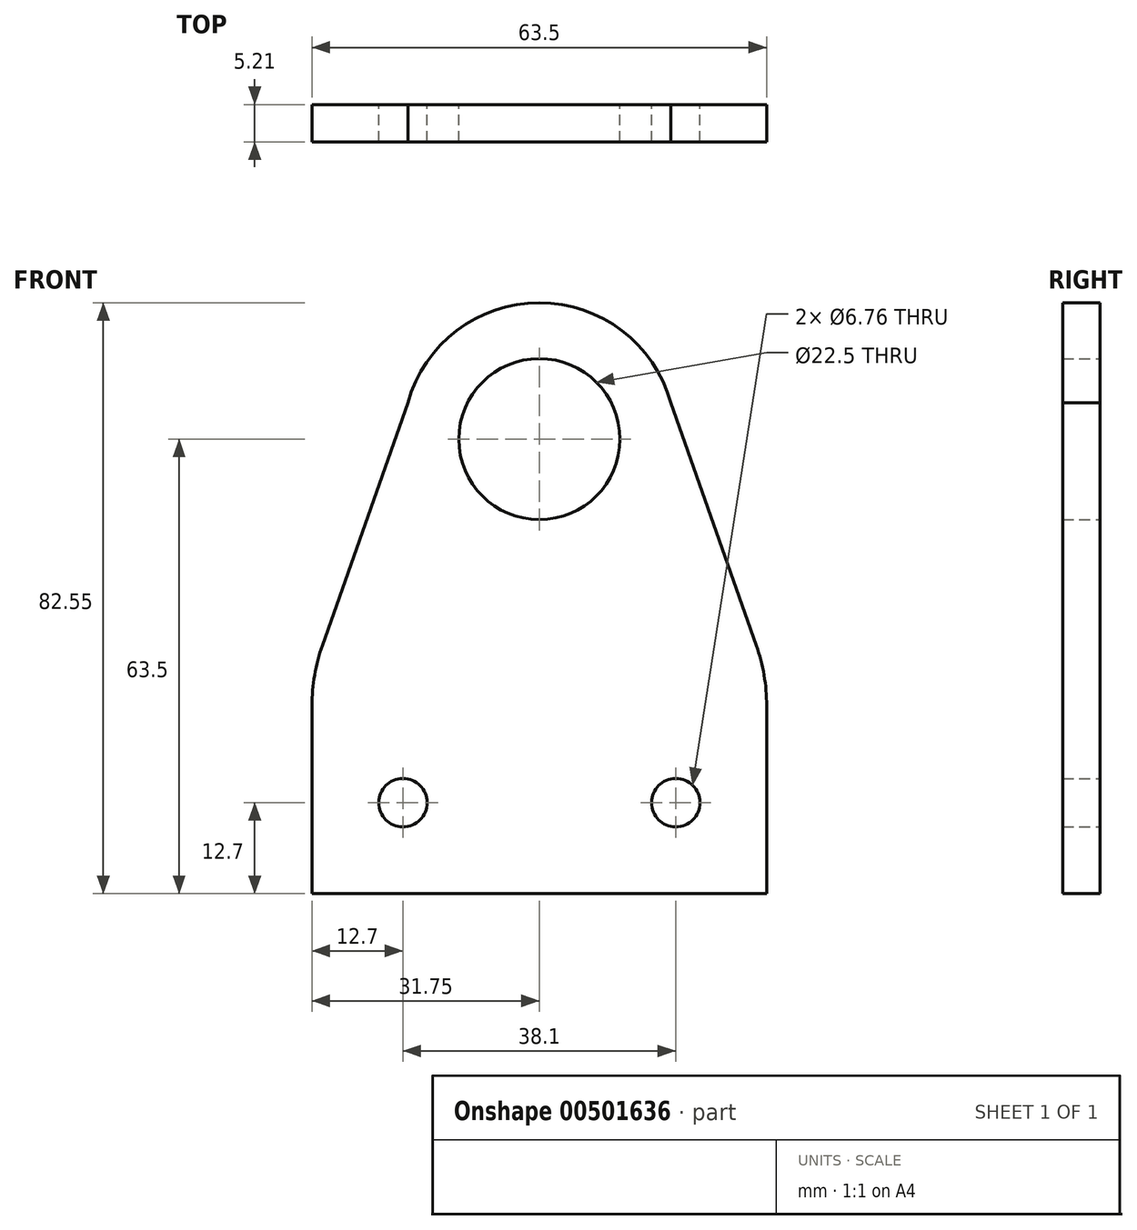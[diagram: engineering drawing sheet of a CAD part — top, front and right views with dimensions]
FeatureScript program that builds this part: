
annotation { "Feature Type Name" : "Feature", "Feature Type Description" : "" }
export const myFeature = defineFeature(function(context is Context, id is Id, definition is map)
    precondition{}
    {
        {
            var Q0;
            Q0=qCreatedBy(makeId("Front.planeOp"),FACE);
            var sketch = newSketch(context, id + "F0", { "sketchPlane" : qUnion([Q0])});
            skLineSegment(sketch, "E0.bottom", {"start": v(-31.75, 0) * mm, "end": v(31.75, 0) * mm});
            skLineSegment(sketch, "E0.left", {"start": v(-31.75, 0) * mm, "end": v(-31.75, 26.24) * mm});
            skLineSegment(sketch, "E0.right", {"start": v(31.75, 0) * mm, "end": v(31.75, 26.24) * mm});
            skCircle(sketch, "E1", {"center": v(0, 63.5) * mm, "radius": 11.25 * mm});
            skLineSegment(sketch, "E2", {"start": v(-31.75, 12.7) * mm, "end": v(31.75, 12.7) * mm, "construction": true});
            skCircle(sketch, "E3", {"center": v(-19.05, 12.7) * mm, "radius": 3.38 * mm});
            skCircle(sketch, "E4", {"center": v(19.05, 12.7) * mm, "radius": 3.38 * mm});
            skArc(sketch, "E5", {"start": v(18.36, 68.58) * mm, "mid": v(0, 82.55) * mm, "end": v(-18.36, 68.58) * mm});
            skLineSegment(sketch, "E6", {"start": v(-30.3, 34.68) * mm, "end": v(-18.36, 68.58) * mm});
            skLineSegment(sketch, "E7.MirrorCS", {"start": v(30.3, 34.68) * mm, "end": v(18.36, 68.58) * mm});
            skPoint(sketch, "E8.visualSharp", {"position": v(-31.75, 30.58) * mm});
            skArc(sketch, "E8.filletArc", {"start": v(-30.3, 34.68) * mm, "mid": v(-31.39, 30.52) * mm, "end": v(-31.75, 26.24) * mm});
            skPoint(sketch, "E9.visualSharp", {"position": v(31.75, 30.58) * mm});
            skArc(sketch, "E9.filletArc", {"start": v(31.75, 26.24) * mm, "mid": v(31.39, 30.52) * mm, "end": v(30.3, 34.68) * mm});
            skPoint(sketch, "E10.visualSharp", {"position": v(-31.75, 0) * mm});
            skLineSegment(sketch, "E10.filletArc", {"start": v(-31.75, 0) * mm, "end": v(-31.75, 0) * mm});
            skSolve(sketch);
        }
        {
            var Q0;
            Q0=makeQuery(id+"F0.imprint","IMPRINT",FACE,{"disambiguationData":[TD([[makeQuery(id+"F0.imprint","IMPRINT",EDGE,{"derivedFrom":sQuery(id+"F0.wireOp",EDGE,"E0.bottom")}),1.0]])]});
            extrude(context, id + "F1", {"entities" : qUnion([Q0]), "depth" : 5.2 * mm});
        }
    });
